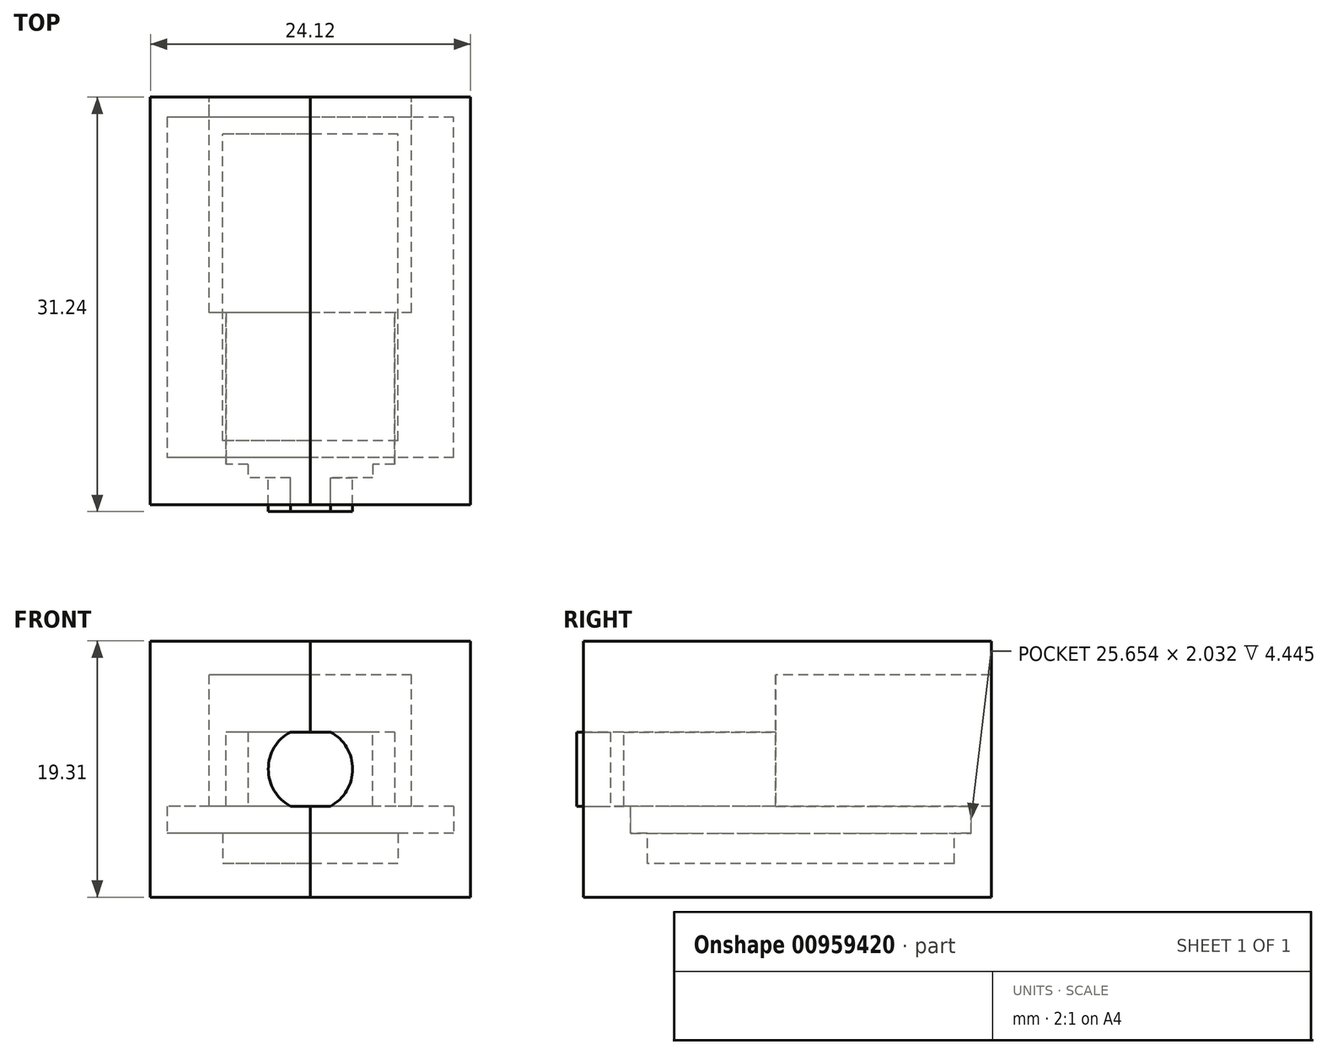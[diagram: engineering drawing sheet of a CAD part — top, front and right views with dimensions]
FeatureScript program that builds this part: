
annotation { "Feature Type Name" : "Feature", "Feature Type Description" : "" }
export const myFeature = defineFeature(function(context is Context, id is Id, definition is map)
    precondition{}
    {
        {
            var Q0;
            Q0=qCreatedBy(makeId("Right.planeOp"),FACE);
            var sketch = newSketch(context, id + "F0", { "sketchPlane" : qUnion([Q0])});
            skLineSegment(sketch, "E0", {"start": v(0, 0) * mm, "end": v(12.83, 0) * mm});
            skLineSegment(sketch, "E1", {"start": v(0, 0) * mm, "end": v(-12.83, 0) * mm});
            skLineSegment(sketch, "E2", {"start": v(0, 0) * mm, "end": v(0, -2.03) * mm});
            skLineSegment(sketch, "E3.bottom", {"start": v(-12.83, 0) * mm, "end": v(12.83, 0) * mm});
            skLineSegment(sketch, "E3.top", {"start": v(-12.83, -2.03) * mm, "end": v(12.83, -2.03) * mm});
            skLineSegment(sketch, "E3.left", {"start": v(-12.83, 0) * mm, "end": v(-12.83, -2.03) * mm});
            skLineSegment(sketch, "E3.right", {"start": v(12.83, 0) * mm, "end": v(12.83, -2.03) * mm});
            skPoint(sketch, "E3.middle", {"position": v(0, -1.02) * mm});
            skLineSegment(sketch, "E4", {"start": v(12.83, -2.03) * mm, "end": v(11.56, -2.03) * mm});
            skLineSegment(sketch, "E5", {"start": v(-12.83, -2.03) * mm, "end": v(-11.56, -2.03) * mm});
            skLineSegment(sketch, "E6", {"start": v(0, -2.03) * mm, "end": v(0, -4.32) * mm});
            skLineSegment(sketch, "E7.bottom", {"start": v(-11.56, -2.03) * mm, "end": v(11.56, -2.03) * mm});
            skLineSegment(sketch, "E7.top", {"start": v(-11.56, -4.32) * mm, "end": v(11.56, -4.32) * mm});
            skLineSegment(sketch, "E7.left", {"start": v(-11.56, -2.03) * mm, "end": v(-11.56, -4.32) * mm});
            skLineSegment(sketch, "E7.right", {"start": v(11.56, -2.03) * mm, "end": v(11.56, -4.32) * mm});
            skPoint(sketch, "E7.middle", {"position": v(0, -3.18) * mm});
            skLineSegment(sketch, "E8", {"start": v(-12.83, 0) * mm, "end": v(-12.83, 5.59) * mm});
            skLineSegment(sketch, "E9", {"start": v(-12.83, 0) * mm, "end": v(-13.34, 0) * mm});
            skLineSegment(sketch, "E10", {"start": v(-13.34, 0) * mm, "end": v(-14.35, 0) * mm});
            skLineSegment(sketch, "E11", {"start": v(-13.34, 0) * mm, "end": v(-13.34, 5.59) * mm});
            skLineSegment(sketch, "E12", {"start": v(-13.34, 5.59) * mm, "end": v(-1.9, 5.59) * mm});
            skLineSegment(sketch, "E13", {"start": v(-1.9, 5.59) * mm, "end": v(-1.9, 0) * mm});
            skLineSegment(sketch, "E14.bottom", {"start": v(-1.9, 5.59) * mm, "end": v(-14.35, 5.59) * mm});
            skLineSegment(sketch, "E14.top", {"start": v(-1.9, 0) * mm, "end": v(-14.35, 0) * mm});
            skLineSegment(sketch, "E14.right", {"start": v(-14.35, 5.59) * mm, "end": v(-14.35, 0) * mm});
            skLineSegment(sketch, "E15", {"start": v(-14.35, 0) * mm, "end": v(-16.38, 0) * mm});
            skLineSegment(sketch, "E16", {"start": v(12.83, 0) * mm, "end": v(14.35, 0) * mm});
            skLineSegment(sketch, "E17", {"start": v(14.35, 0) * mm, "end": v(14.35, 9.9) * mm});
            skLineSegment(sketch, "E18", {"start": v(-1.9, 5.59) * mm, "end": v(-1.9, 9.9) * mm});
            skLineSegment(sketch, "E19", {"start": v(-1.9, 9.9) * mm, "end": v(14.35, 9.9) * mm});
            skLineSegment(sketch, "E20", {"start": v(-11.56, -4.32) * mm, "end": v(-11.56, -6.86) * mm});
            skLineSegment(sketch, "E21", {"start": v(-16.38, 0) * mm, "end": v(-16.38, -6.86) * mm});
            skLineSegment(sketch, "E22", {"start": v(-11.56, -6.86) * mm, "end": v(-16.38, -6.86) * mm});
            skLineSegment(sketch, "E23", {"start": v(14.35, 9.9) * mm, "end": v(14.35, 12.45) * mm});
            skLineSegment(sketch, "E24.bottom", {"start": v(14.35, 12.45) * mm, "end": v(-16.38, 12.45) * mm});
            skLineSegment(sketch, "E24.top", {"start": v(14.35, -6.86) * mm, "end": v(-16.38, -6.86) * mm});
            skLineSegment(sketch, "E24.left", {"start": v(14.35, 12.45) * mm, "end": v(14.35, -6.86) * mm});
            skLineSegment(sketch, "E24.right", {"start": v(-16.38, 12.45) * mm, "end": v(-16.38, -6.86) * mm});
            skSolve(sketch);
        }
        {
            var Q0;
            {var subQ1=sQuery(id+"F0.wireOp",EDGE,"E2");Q0=makeQuery(id+"F0.imprint","IMPRINT",FACE,{"disambiguationData":[TD([[makeQuery(id+"F0.imprint","IMPRINT",EDGE,{"derivedFrom":subQ1}),-1.0]])]});}
            var Q1;
            Q1=makeQuery(id+"F0.imprint","IMPRINT",FACE,{"disambiguationData":[TD([[makeQuery(id+"F0.imprint","IMPRINT",EDGE,{"derivedFrom":sQuery(id+"F0.wireOp",EDGE,"E0")}),-1.0]])]});
            extrude(context, id + "F1", {"entities" : qUnion([Q0, Q1]), "endBound" : BoundingType.SYMMETRIC, "depth" : 21.59 * mm, "offsetDistance" : 25.4 * mm});
        }
        {
            var Q0;
            {var subQ0=sQuery(id+"F0.wireOp",EDGE,"E6");Q0=makeQuery(id+"F0.imprint","IMPRINT",FACE,{"disambiguationData":[TD([[makeQuery(id+"F0.imprint","IMPRINT",EDGE,{"derivedFrom":subQ0}),-1.0]])]});}
            var Q1;
            {var subQ0=sQuery(id+"F0.wireOp",EDGE,"E6");Q1=makeQuery(id+"F0.imprint","IMPRINT",FACE,{"disambiguationData":[TD([[makeQuery(id+"F0.imprint","IMPRINT",EDGE,{"derivedFrom":subQ0}),1.0]])]});}
            extrude(context, id + "F2", {"entities" : qUnion([Q0, Q1]), "operationType" : NewBodyOperationType.ADD, "endBound" : BoundingType.SYMMETRIC, "depth" : 13.2 * mm, "offsetDistance" : 25.4 * mm});
        }
        {
            var Q0;
            {var subQ2=sQuery(id+"F0.wireOp",EDGE,"E0");Q0=makeQuery(id+"F0.imprint","IMPRINT",FACE,{"disambiguationData":[TD([[makeQuery(id+"F0.imprint","IMPRINT",EDGE,{"derivedFrom":subQ2}),1.0]])]});}
            extrude(context, id + "F3", {"entities" : qUnion([Q0]), "operationType" : NewBodyOperationType.ADD, "endBound" : BoundingType.SYMMETRIC, "depth" : 15.24 * mm, "offsetDistance" : 25.4 * mm});
        }
        {
            var Q0;
            {var subQ2=sQuery(id+"F0.wireOp",EDGE,"E8");Q0=makeQuery(id+"F0.imprint","IMPRINT",FACE,{"disambiguationData":[TD([[makeQuery(id+"F0.imprint","IMPRINT",EDGE,{"derivedFrom":subQ2}),-1.0]])]});}
            var Q1;
            {var subQ0=sQuery(id+"F0.wireOp",EDGE,"E8");Q1=makeQuery(id+"F0.imprint","IMPRINT",FACE,{"disambiguationData":[TD([[makeQuery(id+"F0.imprint","IMPRINT",EDGE,{"derivedFrom":subQ0}),1.0]])]});}
            extrude(context, id + "F4", {"entities" : qUnion([Q0, Q1]), "operationType" : NewBodyOperationType.ADD, "endBound" : BoundingType.SYMMETRIC, "depth" : 12.7 * mm, "offsetDistance" : 25.4 * mm});
        }
        {
            var Q0;
            Q0=makeQuery(id+"F0.imprint","IMPRINT",FACE,{"disambiguationData":[TD([[makeQuery(id+"F0.imprint","IMPRINT",EDGE,{"derivedFrom":sQuery(id+"F0.wireOp",EDGE,"E10")}),-1.0]])]});
            extrude(context, id + "F5", {"entities" : qUnion([Q0]), "operationType" : NewBodyOperationType.ADD, "endBound" : BoundingType.SYMMETRIC, "depth" : 9.4 * mm, "offsetDistance" : 25.4 * mm});
        }
        {
            var Q0;
            Q0=makeQuery(id+"F5.opExtrude","SWEPT_FACE",FACE,{"disambiguationData":[OSD([sQuery(id+"F0.wireOp",EDGE,"E14.right")])]});
            var sketch = newSketch(context, id + "F6", { "sketchPlane" : qUnion([Q0])});
            skLineSegment(sketch, "E25", {"start": v(0, 5.59) * mm, "end": v(0, 0) * mm});
            skCircle(sketch, "E26", {"center": v(0, 2.8) * mm, "radius": 3.18 * mm});
            skSolve(sketch);
        }
        {
            var Q0;
            {var subQ0=sQuery(id+"F6.wireOp",EDGE,"E25");Q0=makeQuery(id+"F6.imprint","IMPRINT",FACE,{"disambiguationData":[TD([[makeQuery(id+"F6.imprint","IMPRINT",EDGE,{"derivedFrom":subQ0}),1.0]])]});}
            var Q1;
            {var subQ0=sQuery(id+"F6.wireOp",EDGE,"E25");Q1=makeQuery(id+"F6.imprint","IMPRINT",FACE,{"disambiguationData":[TD([[makeQuery(id+"F6.imprint","IMPRINT",EDGE,{"derivedFrom":subQ0}),-1.0]])]});}
            var Q2;
            {var subQ0=sQuery(id+"F6.wireOp",EDGE,"E26");var subQ1=makeQuery(id+"F5.opExtrude","SWEPT_EDGE",EDGE,{"disambiguationData":[OSD([sQuery(id+"F0.wireOp",EDGE,"E14.bottom"),sQuery(id+"F0.wireOp",EDGE,"E14.right")])]});var subQ2=makeQuery(id+"F6.imprint","INTERSECT",VERTEX,{"disambiguationData":[OD(0.0)],"derivedFrom":[subQ1,subQ0]});Q2=makeQuery(id+"F6.imprint","IMPRINT",FACE,{"disambiguationData":[TD([[makeQuery(id+"F6.imprint","IMPRINT",EDGE,{"disambiguationData":[TD([[subQ2,1.0]])],"derivedFrom":subQ0}),1.0]])]});}
            var Q3;
            {var subQ0=sQuery(id+"F6.wireOp",EDGE,"E26");var subQ1=makeQuery(id+"F5.opExtrude","SWEPT_EDGE",EDGE,{"disambiguationData":[OSD([sQuery(id+"F0.wireOp",EDGE,"E10"),sQuery(id+"F0.wireOp",EDGE,"E14.right"),sQuery(id+"F0.wireOp",EDGE,"E15")])]});var subQ2=makeQuery(id+"F6.imprint","INTERSECT",VERTEX,{"disambiguationData":[OD(0.0)],"derivedFrom":[subQ1,subQ0]});Q3=makeQuery(id+"F6.imprint","IMPRINT",FACE,{"disambiguationData":[TD([[makeQuery(id+"F6.imprint","IMPRINT",EDGE,{"disambiguationData":[TD([[subQ2,-1.0]])],"derivedFrom":subQ0}),1.0]])]});}
            extrude(context, id + "F7", {"entities" : qUnion([Q0, Q1, Q2, Q3]), "depth" : 2.54 * mm, "offsetDistance" : 25.4 * mm});
        }
        {
            var Q0;
            {var subQ0=sQuery(id+"F6.wireOp",EDGE,"E26");var subQ1=makeQuery(id+"F5.opExtrude","SWEPT_EDGE",EDGE,{"disambiguationData":[OSD([sQuery(id+"F0.wireOp",EDGE,"E14.bottom"),sQuery(id+"F0.wireOp",EDGE,"E14.right")])]});var subQ2=makeQuery(id+"F6.imprint","INTERSECT",VERTEX,{"disambiguationData":[OD(0.0)],"derivedFrom":[subQ1,subQ0]});Q0=makeQuery(id+"F6.imprint","IMPRINT",FACE,{"disambiguationData":[TD([[makeQuery(id+"F6.imprint","IMPRINT",EDGE,{"disambiguationData":[TD([[subQ2,1.0]])],"derivedFrom":subQ0}),1.0]])]});}
            var Q1;
            {var subQ0=sQuery(id+"F6.wireOp",EDGE,"E26");var subQ1=makeQuery(id+"F5.opExtrude","SWEPT_EDGE",EDGE,{"disambiguationData":[OSD([sQuery(id+"F0.wireOp",EDGE,"E10"),sQuery(id+"F0.wireOp",EDGE,"E14.right"),sQuery(id+"F0.wireOp",EDGE,"E15")])]});var subQ2=makeQuery(id+"F6.imprint","INTERSECT",VERTEX,{"disambiguationData":[OD(0.0)],"derivedFrom":[subQ1,subQ0]});Q1=makeQuery(id+"F6.imprint","IMPRINT",FACE,{"disambiguationData":[TD([[makeQuery(id+"F6.imprint","IMPRINT",EDGE,{"disambiguationData":[TD([[subQ2,-1.0]])],"derivedFrom":subQ0}),1.0]])]});}
            extrude(context, id + "F8", {"entities" : qUnion([Q0, Q1]), "operationType" : NewBodyOperationType.ADD, "oppositeDirection" : true, "depth" : 1.02 * mm, "offsetDistance" : 25.4 * mm});
        }
        {
            var Q0;
            {var subQ0=sQuery(id+"F0.wireOp",EDGE,"E14.bottom");Q0=makeQuery(id+"F0.imprint","IMPRINT",FACE,{"disambiguationData":[TD([[makeQuery(id+"F0.imprint","IMPRINT",EDGE,{"derivedFrom":subQ0}),-1.0]])]});}
            var Q1;
            {var subQ1=sQuery(id+"F0.wireOp",EDGE,"E3.left");Q1=makeQuery(id+"F0.imprint","IMPRINT",FACE,{"disambiguationData":[TD([[makeQuery(id+"F0.imprint","IMPRINT",EDGE,{"derivedFrom":subQ1}),-1.0]])]});}
            var Q2;
            {var subQ3=sQuery(id+"F0.wireOp",EDGE,"E3.right");Q2=makeQuery(id+"F0.imprint","IMPRINT",FACE,{"disambiguationData":[TD([[makeQuery(id+"F0.imprint","IMPRINT",EDGE,{"derivedFrom":subQ3}),1.0]])]});}
            var Q3;
            Q3=makeQuery(id+"F0.imprint","IMPRINT",FACE,{"disambiguationData":[TD([[makeQuery(id+"F0.imprint","IMPRINT",EDGE,{"derivedFrom":sQuery(id+"F0.wireOp",EDGE,"E10")}),-1.0]])]});
            var Q4;
            {var subQ2=sQuery(id+"F0.wireOp",EDGE,"E8");Q4=makeQuery(id+"F0.imprint","IMPRINT",FACE,{"disambiguationData":[TD([[makeQuery(id+"F0.imprint","IMPRINT",EDGE,{"derivedFrom":subQ2}),-1.0]])]});}
            var Q5;
            {var subQ0=sQuery(id+"F0.wireOp",EDGE,"E8");Q5=makeQuery(id+"F0.imprint","IMPRINT",FACE,{"disambiguationData":[TD([[makeQuery(id+"F0.imprint","IMPRINT",EDGE,{"derivedFrom":subQ0}),1.0]])]});}
            var Q6;
            {var subQ1=sQuery(id+"F0.wireOp",EDGE,"E2");Q6=makeQuery(id+"F0.imprint","IMPRINT",FACE,{"disambiguationData":[TD([[makeQuery(id+"F0.imprint","IMPRINT",EDGE,{"derivedFrom":subQ1}),-1.0]])]});}
            var Q7;
            {var subQ0=sQuery(id+"F0.wireOp",EDGE,"E6");Q7=makeQuery(id+"F0.imprint","IMPRINT",FACE,{"disambiguationData":[TD([[makeQuery(id+"F0.imprint","IMPRINT",EDGE,{"derivedFrom":subQ0}),-1.0]])]});}
            var Q8;
            {var subQ0=sQuery(id+"F0.wireOp",EDGE,"E6");Q8=makeQuery(id+"F0.imprint","IMPRINT",FACE,{"disambiguationData":[TD([[makeQuery(id+"F0.imprint","IMPRINT",EDGE,{"derivedFrom":subQ0}),1.0]])]});}
            var Q9;
            Q9=makeQuery(id+"F0.imprint","IMPRINT",FACE,{"disambiguationData":[TD([[makeQuery(id+"F0.imprint","IMPRINT",EDGE,{"derivedFrom":sQuery(id+"F0.wireOp",EDGE,"E0")}),-1.0]])]});
            var Q10;
            {var subQ2=sQuery(id+"F0.wireOp",EDGE,"E0");Q10=makeQuery(id+"F0.imprint","IMPRINT",FACE,{"disambiguationData":[TD([[makeQuery(id+"F0.imprint","IMPRINT",EDGE,{"derivedFrom":subQ2}),1.0]])]});}
            extrude(context, id + "F9", {"entities" : qUnion([Q0, Q1, Q2, Q3, Q4, Q5, Q6, Q7, Q8, Q9, Q10]), "depth" : 12.06 * mm, "offsetDistance" : 25.4 * mm});
        }
        {
            var Q0;
            {var subQ0=sQuery(id+"F0.wireOp",EDGE,"E14.bottom");Q0=makeQuery(id+"F0.imprint","IMPRINT",FACE,{"disambiguationData":[TD([[makeQuery(id+"F0.imprint","IMPRINT",EDGE,{"derivedFrom":subQ0}),-1.0]])]});}
            var Q1;
            {var subQ2=sQuery(id+"F0.wireOp",EDGE,"E0");Q1=makeQuery(id+"F0.imprint","IMPRINT",FACE,{"disambiguationData":[TD([[makeQuery(id+"F0.imprint","IMPRINT",EDGE,{"derivedFrom":subQ2}),1.0]])]});}
            var Q2;
            {var subQ2=sQuery(id+"F0.wireOp",EDGE,"E8");Q2=makeQuery(id+"F0.imprint","IMPRINT",FACE,{"disambiguationData":[TD([[makeQuery(id+"F0.imprint","IMPRINT",EDGE,{"derivedFrom":subQ2}),-1.0]])]});}
            var Q3;
            {var subQ0=sQuery(id+"F0.wireOp",EDGE,"E8");Q3=makeQuery(id+"F0.imprint","IMPRINT",FACE,{"disambiguationData":[TD([[makeQuery(id+"F0.imprint","IMPRINT",EDGE,{"derivedFrom":subQ0}),1.0]])]});}
            var Q4;
            Q4=makeQuery(id+"F0.imprint","IMPRINT",FACE,{"disambiguationData":[TD([[makeQuery(id+"F0.imprint","IMPRINT",EDGE,{"derivedFrom":sQuery(id+"F0.wireOp",EDGE,"E10")}),-1.0]])]});
            var Q5;
            {var subQ1=sQuery(id+"F0.wireOp",EDGE,"E3.left");Q5=makeQuery(id+"F0.imprint","IMPRINT",FACE,{"disambiguationData":[TD([[makeQuery(id+"F0.imprint","IMPRINT",EDGE,{"derivedFrom":subQ1}),-1.0]])]});}
            var Q6;
            {var subQ1=sQuery(id+"F0.wireOp",EDGE,"E2");Q6=makeQuery(id+"F0.imprint","IMPRINT",FACE,{"disambiguationData":[TD([[makeQuery(id+"F0.imprint","IMPRINT",EDGE,{"derivedFrom":subQ1}),-1.0]])]});}
            var Q7;
            {var subQ0=sQuery(id+"F0.wireOp",EDGE,"E6");Q7=makeQuery(id+"F0.imprint","IMPRINT",FACE,{"disambiguationData":[TD([[makeQuery(id+"F0.imprint","IMPRINT",EDGE,{"derivedFrom":subQ0}),-1.0]])]});}
            var Q8;
            {var subQ3=sQuery(id+"F0.wireOp",EDGE,"E3.right");Q8=makeQuery(id+"F0.imprint","IMPRINT",FACE,{"disambiguationData":[TD([[makeQuery(id+"F0.imprint","IMPRINT",EDGE,{"derivedFrom":subQ3}),1.0]])]});}
            var Q9;
            {var subQ0=sQuery(id+"F0.wireOp",EDGE,"E6");Q9=makeQuery(id+"F0.imprint","IMPRINT",FACE,{"disambiguationData":[TD([[makeQuery(id+"F0.imprint","IMPRINT",EDGE,{"derivedFrom":subQ0}),1.0]])]});}
            var Q10;
            Q10=makeQuery(id+"F0.imprint","IMPRINT",FACE,{"disambiguationData":[TD([[makeQuery(id+"F0.imprint","IMPRINT",EDGE,{"derivedFrom":sQuery(id+"F0.wireOp",EDGE,"E0")}),-1.0]])]});
            extrude(context, id + "F10", {"entities" : qUnion([Q0, Q1, Q2, Q3, Q4, Q5, Q6, Q7, Q8, Q9, Q10]), "oppositeDirection" : true, "depth" : 12.06 * mm, "offsetDistance" : 25.4 * mm});
        }
        {
            var Q0;
            Q0=makeQuery(id+"F1.opExtrude","SWEPT_BODY",BODY,{"disambiguationData":[OSD([sQuery(id+"F0.wireOp",EDGE,"E0"),sQuery(id+"F0.wireOp",EDGE,"E1"),sQuery(id+"F0.wireOp",EDGE,"E3.top"),sQuery(id+"F0.wireOp",EDGE,"E3.left"),sQuery(id+"F0.wireOp",EDGE,"E3.right")])]});
            var Q1;
            Q1=makeQuery(id+"F7.opExtrude","SWEPT_BODY",BODY,{"disambiguationData":[OSD([sQuery(id+"F6.wireOp",EDGE,"E26")])]});
            var Q2;
            Q2=makeQuery(id+"F10.opExtrude","SWEPT_BODY",BODY,{"disambiguationData":[OSD([sQuery(id+"F0.wireOp",EDGE,"E17"),sQuery(id+"F0.wireOp",EDGE,"E21"),sQuery(id+"F0.wireOp",EDGE,"E22"),sQuery(id+"F0.wireOp",EDGE,"E23"),sQuery(id+"F0.wireOp",EDGE,"E24.bottom"),sQuery(id+"F0.wireOp",EDGE,"E24.top"),sQuery(id+"F0.wireOp",EDGE,"E24.left"),sQuery(id+"F0.wireOp",EDGE,"E24.right")])]});
            var Q3;
            Q3=makeQuery(id+"F9.opExtrude","SWEPT_BODY",BODY,{"disambiguationData":[OSD([sQuery(id+"F0.wireOp",EDGE,"E17"),sQuery(id+"F0.wireOp",EDGE,"E21"),sQuery(id+"F0.wireOp",EDGE,"E22"),sQuery(id+"F0.wireOp",EDGE,"E23"),sQuery(id+"F0.wireOp",EDGE,"E24.bottom"),sQuery(id+"F0.wireOp",EDGE,"E24.top"),sQuery(id+"F0.wireOp",EDGE,"E24.left"),sQuery(id+"F0.wireOp",EDGE,"E24.right")])]});
            booleanBodies(context, id + "F11", {"operationType" : BooleanOperationType.SUBTRACTION, "tools" : qUnion([Q0, Q1]), "targets" : qUnion([Q2, Q3]), "keepTools" : true});
        }
    });
